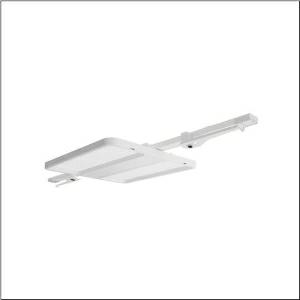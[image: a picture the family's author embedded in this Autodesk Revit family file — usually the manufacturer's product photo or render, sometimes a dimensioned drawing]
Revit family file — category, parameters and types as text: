
# Revit family: highbay_11_fur_modario_r__tragschiene_midi_51hn12da5mma_2f69
name_source: partatom
category: Lighting Fixtures
units: mm (PartAtom-declared; Revit-internal decimal feet)

## family parameters
Cut with Voids When Loaded = No
Host = Face
Light Source = No
Part Type = Normal
Room Calculation Point = No
Round Connector Dimension = Use Diameter
Shared = No

## types (1)
- --- (1 x LED, 27890 lm, 146.6 W, 5000K)
    Apparent Load = 147 VA
    CIE Flux Codes = 87 98 100 100 100
    Color Rendering = 80
    Color Temperature = 5000K
    Default Elevation = 1800 mm
    Description = high bay luminaire Highbay 11 for Modario® trunking rail midi; direct symmetric wide distribution, light control with lens of PMMA; UGR ≤ 22 (X = 4H | Y = 8H | S = 0.25H | reflection values 70/50/20); luminous flux: 27.890lm; light colour: 850, colour temperature: 5000K, MacAdam ≤ 2 SDCM (initial), colour rendering: CRI > 80; luminous efficacy: 190,2lm/W; rated service life: 100.000h (L95/B50) at AT= 25°C; control: DALI 2; luminaire connection: plug, 5-pole, with phase selectionmains connection: 230..240V, AC 50/60Hz; connected load: 146,6W; protection rating (complete): IP64; insulation class (complete): insulation class I (protective earthing); protection symbol: D; impact resistance: IK07; certification: CE, ENEC, VDE, UKCA; internal wiring halogen-free; luminaire corresponds to IFS (International Featured Standards) requirements for safety and quality in the food industry; LABS conformity tested according to VDMA 24364:2018-05; housing frame of high-performance plastic PA6, matt traffic white (RAL 9016); cover of PMMA; fixing on rail side of steel, galvanised, white; blank cover of PC, traffic white (RAL 9016); dimension (LxWxH): 1.195 x 442 x 72mm; permissible operating ambient temperature: -40..+50°C (reducing of maximum allowable ambient temperature of 5°C with ceiling mounting); packaging unit: 1 piece
    Height = 72 mm  [stored 0.23622 ft]
    Lamp = 1 x LED
    Lamp Light Flux = 27890 lm
    Lamp Power = 146.6 W
    Lamp count = 1
    Length = 474 mm
    Luminous efficacy = 190 lm/W
    Manufacturer = Siteco
    ModVariant = No
    Model = 51HN12DA5MMA
    Mounting Place = Ceiling
    Mounting Type = Pendant
    Number of Poles = 1
    OnlyDefault = Yes
    Power Factor = 1
    Product Name = Highbay 11 für Modario® Tragschiene midi
    Product group = high bay luminaire
    ProductGroupID = 901
    Protection Class = Protection class I
    Protection Degree = IP 64
    RLX_Detail_Level = 1
    RLX_Emergency_Light_Flux = 0 lm
    RLX_Emergency_Type = 0
    RLX_Emergency_Type_DB = No
    RlxData = <blob elided: 18125 chars, md5=7db575c1>
    Socket = socket
    Standby Power = 0 W
    System Light Flux = 27891 lm
    System Power = 147 W
    Type Comments = factory setting: luminous flux: 100 % | dim-lin: 254 | 661 mA
    Type Image = l_1363266.jpg
    URL = http://relux.com
    VarID = @adj_007935
    Voltage = 0 V
    Weight = 0.00 kg
    Width = 442 mm

note: [stored X ft] marks values corroborated as IEEE doubles in the binary element streams (Revit-internal decimal feet)

## geometry (parser evidence)
native form markers: Blend x4, Sweep x11
no freeform markers — native parametric forms only
